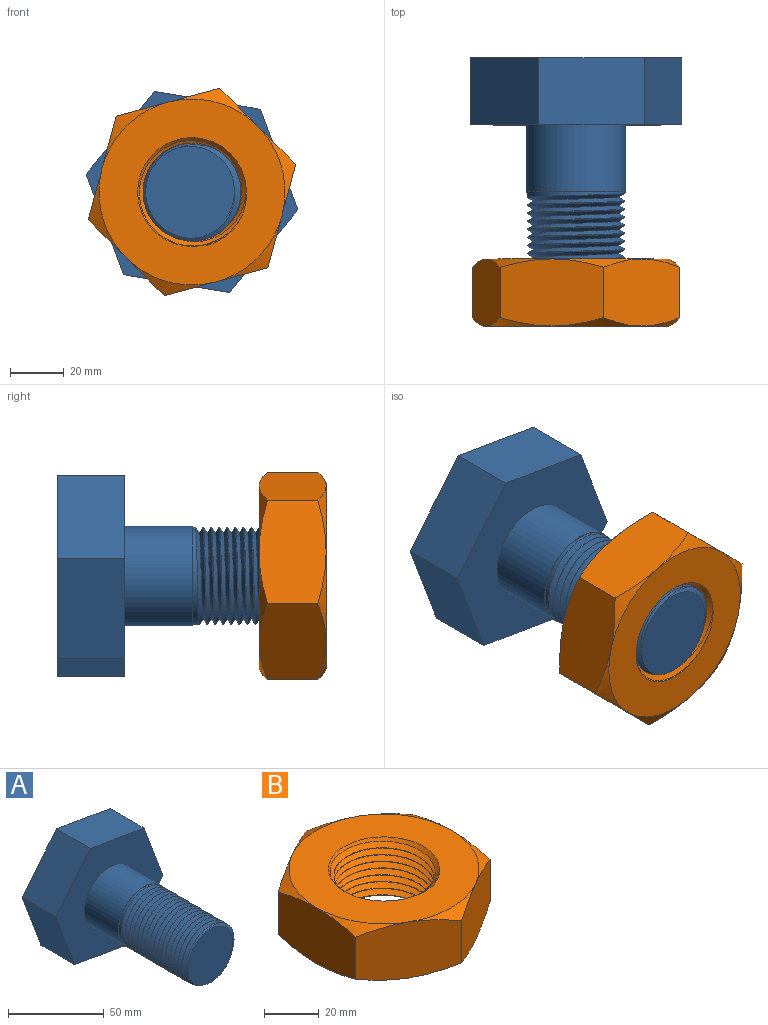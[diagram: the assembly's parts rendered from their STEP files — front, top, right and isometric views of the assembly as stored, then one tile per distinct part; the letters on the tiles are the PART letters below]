
ASSEMBLY  parts=2 mates=1
PART A: 31 faces, bbox 79.6x102.6x75.8 mm
  f0: plane 30.8x25.52mm, normal (0.77,0,-0.64), area 1000mm2, adj f1,f5,f6,f7
  f1: plane 37.5x25mm, normal (0.94,0,0.35), area 1000mm2, adj f0,f2,f6,f7
  f2: plane 39.44x25mm, normal (0.17,0,0.99), area 1000mm2, adj f1,f3,f6,f7
  f3: plane 30.8x25.52mm, normal (-0.77,0,0.64), area 1000mm2, adj f2,f4,f6,f7
  f4: plane 37.5x25mm, normal (-0.94,0,-0.35), area 1000mm2, adj f3,f5,f6,f7
  f5: plane 39.44x25mm, normal (-0.17,0,-0.99), area 1000mm2, adj f0,f4,f6,f7
  f6: plane 78.87x75mm, normal (0,-1,0), area 3081.7mm2, adj f0,f1,f2,f3,f4,f5,f8
  f7: plane 78.87x75mm, normal (0,1,0), area 4156.9mm2, adj f0,f1,f2,f3,f4,f5
  f8: cylinder r=18.5mm len=37mm, axis (0,1,0), area 2906mm2, adj f6,f9
  f9: plane 37x37mm, normal (0,-1,0), area 28.9mm2, adj f8,f25
  f10: cylinder r=18.25mm len=36.5mm, axis (0,1,0), area 22.2mm2, adj f11,f27,f29,f30
  f11: cylinder r=18.25mm len=36.5mm, axis (0,1,0), area 22.9mm2, adj f10,f12,f29,f30
  f12: cylinder r=18.25mm len=36.5mm, axis (0,1,0), area 23mm2, adj f11,f13,f29,f30
  f13: cylinder r=18.25mm len=36.5mm, axis (0,1,0), area 22.9mm2, adj f12,f14,f29,f30
  f14: cylinder r=18.25mm len=36.5mm, axis (0,1,0), area 22.9mm2, adj f13,f15,f29,f30
  f15: cylinder r=18.25mm len=36.5mm, axis (0,1,0), area 23mm2, adj f14,f16,f29,f30
  f16: cylinder r=18.25mm len=36.5mm, axis (0,1,0), area 22.9mm2, adj f15,f17,f29,f30
  f17: cylinder r=18.25mm len=36.5mm, axis (0,1,0), area 22.9mm2, adj f16,f18,f29,f30
  f18: cylinder r=18.25mm len=36.5mm, axis (0,1,0), area 22.9mm2, adj f17,f19,f29,f30
  f19: cylinder r=18.25mm len=36.5mm, axis (0,1,0), area 22.9mm2, adj f18,f20,f29,f30
  f20: cylinder r=18.25mm len=36.5mm, axis (0,1,0), area 22.9mm2, adj f19,f21,f29,f30
  f21: cylinder r=18.25mm len=36.5mm, axis (0,1,0), area 22.9mm2, adj f20,f22,f29,f30
  f22: cylinder r=18.25mm len=36.5mm, axis (0,1,0), area 23mm2, adj f21,f23,f29,f30
  f23: cylinder r=18.25mm len=36.5mm, axis (0,1,0), area 22.9mm2, adj f22,f24,f29,f30
  f24: cylinder r=18.25mm len=36.5mm, axis (0,1,0), area 22.9mm2, adj f23,f25,f29,f30
  f25: cylinder r=18.25mm len=36.5mm, axis (0,1,0), area 183.5mm2, adj f9,f24,f28,f29,f30
  f26: plane 35.04x34mm, normal (0,-1,0), area 893.6mm2, adj f27,f29,f30
  f27: cone r=17.25mm half-angle=45deg, axis (0,1,0), area 40.8mm2, adj f10,f26,f29,f30
  f28: plane 2.8x2.1mm, normal (0.87,0,0.5), area 3.4mm2, adj f25,f29,f30
  f29: bspline ~51.4x42.15mm, area 4904.9mm2, adj f10,f11,f12,f13,f14,f15,f16,f17
  f30: bspline ~50.9x42.15mm, area 4767.1mm2, adj f10,f11,f12,f13,f14,f15,f16,f17
PART B: 24 faces, bbox 81.7x81.7x30 mm
  f0: plane 70.96x70.96mm, normal (0,0,-1), area 2588.2mm2, adj f1,f3,f4,f7,f9,f11,f13,f22
  f1: cylinder r=18.25mm len=36.5mm, axis (0,0,-1), area 493.4mm2, adj f0,f21,f22,f23
  f2: plane 69.37x69.37mm, normal (0,0,1), area 2477.2mm2, adj f5,f6,f8,f10,f12,f14,f21,f22
  f3: cone r=53.95mm half-angle=60deg, axis (0,0,1), area 74.5mm2, adj f0,f15,f20
  f4: cone r=53.95mm half-angle=60deg, axis (0,0,1), area 74.5mm2, adj f0,f15,f16
  f5: cone r=53.95mm half-angle=60deg, axis (0,0,-1), area 74.5mm2, adj f2,f15,f20
  f6: cone r=53.95mm half-angle=60deg, axis (0,0,-1), area 74.5mm2, adj f2,f15,f16
  f7: cone r=53.95mm half-angle=60deg, axis (0,0,1), area 74.5mm2, adj f0,f16,f17
  f8: cone r=53.95mm half-angle=60deg, axis (0,0,-1), area 74.5mm2, adj f2,f16,f17
  f9: cone r=53.95mm half-angle=60deg, axis (0,0,1), area 74.5mm2, adj f0,f17,f18
  f10: cone r=53.95mm half-angle=60deg, axis (0,0,-1), area 74.5mm2, adj f2,f17,f18
  f11: cone r=53.95mm half-angle=60deg, axis (0,0,1), area 74.5mm2, adj f0,f18,f19
  f12: cone r=53.95mm half-angle=60deg, axis (0,0,-1), area 74.5mm2, adj f2,f18,f19
  f13: cone r=53.95mm half-angle=60deg, axis (0,0,1), area 74.5mm2, adj f0,f19,f20
  f14: cone r=53.95mm half-angle=60deg, axis (0,0,-1), area 74.5mm2, adj f2,f19,f20
  f15: plane 34.64x25.01mm, normal (0.5,-0.87,0), area 915.1mm2, adj f3,f4,f5,f6,f16,f20
  f16: plane 34.64x25.01mm, normal (-0.5,-0.87,0), area 915.1mm2, adj f4,f6,f7,f8,f15,f17
  f17: plane 40.01x25.01mm, normal (-1,0,0), area 915.1mm2, adj f7,f8,f9,f10,f16,f18
  f18: plane 34.64x25.01mm, normal (-0.5,0.87,0), area 915.1mm2, adj f9,f10,f11,f12,f17,f19
  f19: plane 34.64x25.01mm, normal (0.5,0.87,0), area 915.1mm2, adj f11,f12,f13,f14,f18,f20
  f20: plane 40.01x25.01mm, normal (1,0,0), area 915.1mm2, adj f3,f5,f13,f14,f15,f19
  f21: cone r=18.25mm half-angle=45deg, axis (0,0,1), area 156.6mm2, adj f1,f2,f22,f23
  f22: bspline ~47.75x41.35mm, area 2764mm2, adj f0,f1,f2,f21,f23
  f23: bspline ~47.75x41.35mm, area 2775.3mm2, adj f0,f1,f2,f21,f22
PLACE A t=(-8.77,38.68,-10.66)mm
PLACE B rot(axis=(0.86,-0.36,0.36),98.4deg) t=(-8.77,-36.32,-10.66)mm
MATE revolute B.f1 <-> A.f8  axis (0,-1,0) through (-8.77,-61.32,-10.66)mm
